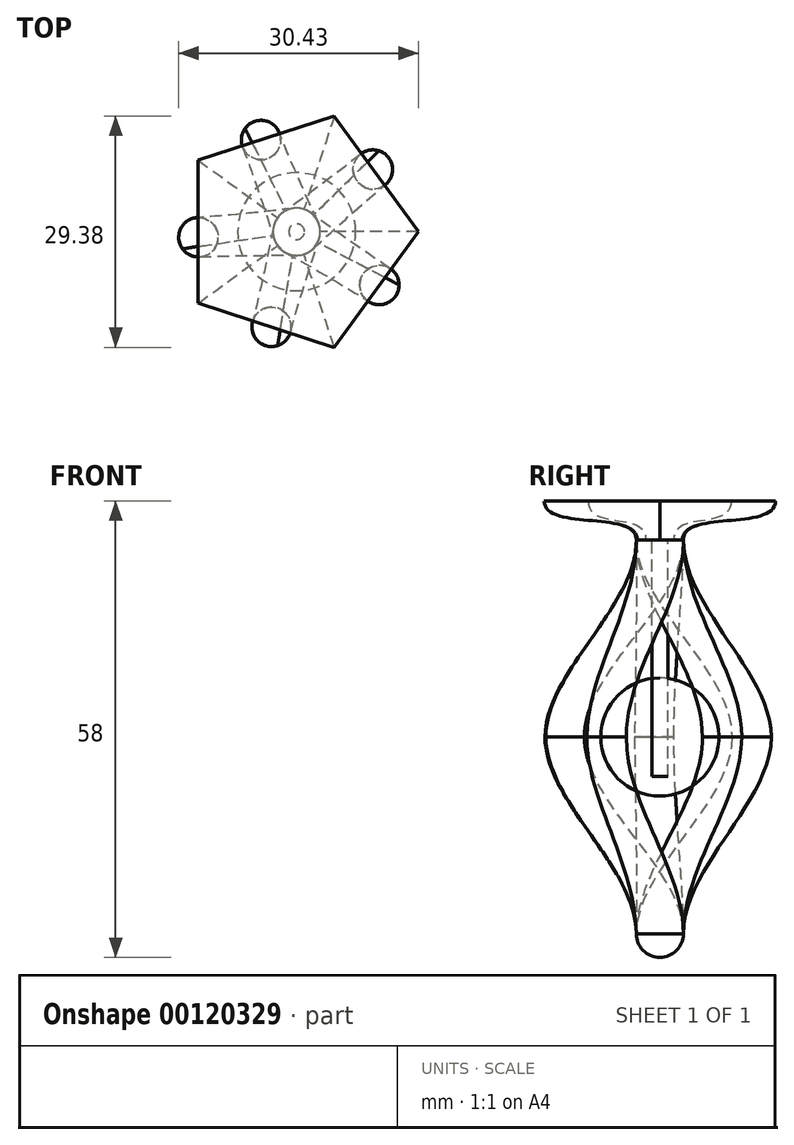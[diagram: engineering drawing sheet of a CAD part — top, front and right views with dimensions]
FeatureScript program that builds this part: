
annotation { "Feature Type Name" : "Feature", "Feature Type Description" : "" }
export const myFeature = defineFeature(function(context is Context, id is Id, definition is map)
    precondition{}
    {
        {
            var Q0;
            Q0=qCreatedBy(makeId("Top.planeOp"),FACE);
            var sketch = newSketch(context, id + "F12", { "sketchPlane" : qUnion([Q0])});
            skCircle(sketch, "E0.cCircle", {"center": v(0, 0) * mm, "radius": 12.5 * mm, "construction": true});
            skCircle(sketch, "E1", {"center": v(10.5, -6.77) * mm, "radius": 2.5 * mm});
            skSolve(sketch);
        }
        {
            var Q0;
            Q0=qCreatedBy(makeId("Top.planeOp"),FACE);
            cPlane(context, id + "F0", {"entities" : qUnion([Q0]), "cplaneType" : CPlaneType.OFFSET, "offset" : 25 * mm, "width" : 150 * mm, "height" : 150 * mm});
        }
        {
            var Q0;
            Q0=qCreatedBy(id+"F0.planeOp",FACE);
            var sketch = newSketch(context, id + "F13", { "sketchPlane" : qUnion([Q0])});
            skCircle(sketch, "E2", {"center": v(0, 0) * mm, "radius": 3 * mm});
            skSolve(sketch);
        }
        {
            var Q0;
            Q0=makeQuery(id+"F12.imprint","IMPRINT",FACE,{"disambiguationData":[TD([[makeQuery(id+"F12.imprint","IMPRINT",EDGE,{"derivedFrom":sQuery(id+"F12.wireOp",EDGE,"E1")}),1.0]])]});
            var Q1;
            Q1=makeQuery(id+"F13.imprint","IMPRINT",FACE,{"disambiguationData":[TD([[makeQuery(id+"F13.imprint","IMPRINT",EDGE,{"derivedFrom":sQuery(id+"F13.wireOp",EDGE,"E2")}),1.0]])]});
            loft(context, id + "F1", {"startCondition" : LoftEndDerivativeType.NORMAL_TO_PROFILE, "startMagnitude" : 1, "endCondition" : LoftEndDerivativeType.NORMAL_TO_PROFILE, "endMagnitude" : 1, "sheetProfilesArray" : [{ "sheetProfileEntities" : qUnion([Q0]) }, { "sheetProfileEntities" : qUnion([Q1]) }]});
        }
        {
            var Q0;
            Q0=makeQuery(id+"F1.opLoft","SWEPT_BODY",BODY,{"disambiguationData":[OSD([makeQuery(id+"F12.imprint","IMPRINT",FACE,{"disambiguationData":[TD([[makeQuery(id+"F12.imprint","IMPRINT",EDGE,{"derivedFrom":sQuery(id+"F12.wireOp",EDGE,"E1")}),1.0]])]}),makeQuery(id+"F13.imprint","IMPRINT",FACE,{"disambiguationData":[TD([[makeQuery(id+"F13.imprint","IMPRINT",EDGE,{"derivedFrom":sQuery(id+"F13.wireOp",EDGE,"E2")}),1.0]])]})])]});
            var Q1;
            Q1=sQuery(id+"F12.wireOp",EDGE,"E0.cCircle");
            circularPattern(context, id + "F2", {"entities" : qUnion([Q0]), "axis" : qUnion([Q1]), "angle" : 72 * degree, "instanceCount" : 5});
        }
        {
            var Q0;
            Q0=makeQuery(id+"F1.opLoft","SWEPT_BODY",BODY,{"disambiguationData":[OSD([makeQuery(id+"F12.imprint","IMPRINT",FACE,{"disambiguationData":[TD([[makeQuery(id+"F12.imprint","IMPRINT",EDGE,{"derivedFrom":sQuery(id+"F12.wireOp",EDGE,"E1")}),1.0]])]}),makeQuery(id+"F13.imprint","IMPRINT",FACE,{"disambiguationData":[TD([[makeQuery(id+"F13.imprint","IMPRINT",EDGE,{"derivedFrom":sQuery(id+"F13.wireOp",EDGE,"E2")}),1.0]])]})])]});
            var Q1;
            Q1=makeQuery(id+"F2.opPattern","COPY",BODY,{"derivedFrom":makeQuery(id+"F1.opLoft","SWEPT_BODY",BODY,{"disambiguationData":[OSD([makeQuery(id+"F12.imprint","IMPRINT",FACE,{"disambiguationData":[TD([[makeQuery(id+"F12.imprint","IMPRINT",EDGE,{"derivedFrom":sQuery(id+"F12.wireOp",EDGE,"E1")}),1.0]])]}),makeQuery(id+"F13.imprint","IMPRINT",FACE,{"disambiguationData":[TD([[makeQuery(id+"F13.imprint","IMPRINT",EDGE,{"derivedFrom":sQuery(id+"F13.wireOp",EDGE,"E2")}),1.0]])]})])]}),"instanceName":"1"});
            var Q2;
            Q2=makeQuery(id+"F2.opPattern","COPY",BODY,{"derivedFrom":makeQuery(id+"F1.opLoft","SWEPT_BODY",BODY,{"disambiguationData":[OSD([makeQuery(id+"F12.imprint","IMPRINT",FACE,{"disambiguationData":[TD([[makeQuery(id+"F12.imprint","IMPRINT",EDGE,{"derivedFrom":sQuery(id+"F12.wireOp",EDGE,"E1")}),1.0]])]}),makeQuery(id+"F13.imprint","IMPRINT",FACE,{"disambiguationData":[TD([[makeQuery(id+"F13.imprint","IMPRINT",EDGE,{"derivedFrom":sQuery(id+"F13.wireOp",EDGE,"E2")}),1.0]])]})])]}),"instanceName":"4"});
            var Q3;
            Q3=makeQuery(id+"F2.opPattern","COPY",BODY,{"derivedFrom":makeQuery(id+"F1.opLoft","SWEPT_BODY",BODY,{"disambiguationData":[OSD([makeQuery(id+"F12.imprint","IMPRINT",FACE,{"disambiguationData":[TD([[makeQuery(id+"F12.imprint","IMPRINT",EDGE,{"derivedFrom":sQuery(id+"F12.wireOp",EDGE,"E1")}),1.0]])]}),makeQuery(id+"F13.imprint","IMPRINT",FACE,{"disambiguationData":[TD([[makeQuery(id+"F13.imprint","IMPRINT",EDGE,{"derivedFrom":sQuery(id+"F13.wireOp",EDGE,"E2")}),1.0]])]})])]}),"instanceName":"3"});
            var Q4;
            Q4=makeQuery(id+"F2.opPattern","COPY",BODY,{"derivedFrom":makeQuery(id+"F1.opLoft","SWEPT_BODY",BODY,{"disambiguationData":[OSD([makeQuery(id+"F12.imprint","IMPRINT",FACE,{"disambiguationData":[TD([[makeQuery(id+"F12.imprint","IMPRINT",EDGE,{"derivedFrom":sQuery(id+"F12.wireOp",EDGE,"E1")}),1.0]])]}),makeQuery(id+"F13.imprint","IMPRINT",FACE,{"disambiguationData":[TD([[makeQuery(id+"F13.imprint","IMPRINT",EDGE,{"derivedFrom":sQuery(id+"F13.wireOp",EDGE,"E2")}),1.0]])]})])]}),"instanceName":"2"});
            var Q5;
            Q5=qCreatedBy(makeId("Top.planeOp"),FACE);
            mirror(context, id + "F14", {"entities" : qUnion([Q0, Q1, Q2, Q3, Q4]), "mirrorPlane" : qUnion([Q5])});
        }
        {
            var Q0;
            Q0=qCreatedBy(makeId("Right.planeOp"),FACE);
            var sketch = newSketch(context, id + "F3", { "sketchPlane" : qUnion([Q0])});
            skLineSegment(sketch, "E3", {"start": v(0, 29.68) * mm, "end": v(0, -30.32) * mm});
            skSolve(sketch);
        }
        {
            var Q0;
            Q0=qCreatedBy(makeId("Right.planeOp"),FACE);
            var sketch = newSketch(context, id + "F15", { "sketchPlane" : qUnion([Q0])});
            skEllipticalArc(sketch, "E4", {});
            skLineSegment(sketch, "E5", {"start": v(0, 7.5) * mm, "end": v(0, -7.5) * mm});
            const initialGuessFycGdjQH3IecEFOBE_1  = {"E4": [0, 0, 0, 1, 0.0075, 0.0075, 0, 3.141592653589793]};
            skSetInitialGuess(sketch, initialGuessFycGdjQH3IecEFOBE_1);
            skSolve(sketch);
        }
        {
            var Q0;
            Q0=makeQuery(id+"F15.imprint","IMPRINT",FACE,{"disambiguationData":[TD([[makeQuery(id+"F15.imprint","IMPRINT",EDGE,{"derivedFrom":sQuery(id+"F15.wireOp",EDGE,"E4")}),1.0]])]});
            var Q1;
            Q1=sQuery(id+"F3.wireOp",EDGE,"E3");
            revolve(context, id + "F4", {"entities" : qUnion([Q0]), "axis" : qUnion([Q1]), "revolveType" : RevolveType.FULL});
        }
        {
            var Q0;
            Q0=makeQuery(id+"F2.opPattern","COPY",FACE,{"derivedFrom":makeQuery(id+"F1.opLoft","CAP_FACE",FACE,{"disambiguationData":[OSD([makeQuery(id+"F13.imprint","IMPRINT",FACE,{"disambiguationData":[TD([[makeQuery(id+"F13.imprint","IMPRINT",EDGE,{"derivedFrom":sQuery(id+"F13.wireOp",EDGE,"E2")}),1.0]])]})])],"isStart":true}),"instanceName":"1"});
            var sketch = newSketch(context, id + "F5", { "sketchPlane" : qUnion([Q0])});
            skCircle(sketch, "E6", {"center": v(0, 0) * mm, "radius": 1 * mm});
            skSolve(sketch);
        }
        {
            var Q0;
            Q0=qCreatedBy(id+"F0.planeOp",FACE);
            cPlane(context, id + "F6", {"entities" : qUnion([Q0]), "cplaneType" : CPlaneType.OFFSET, "offset" : 5 * mm, "width" : 150 * mm, "height" : 150 * mm});
        }
        {
            var Q0;
            Q0=qCreatedBy(id+"F6.planeOp",FACE);
            var sketch = newSketch(context, id + "F7", { "sketchPlane" : qUnion([Q0])});
            skCircle(sketch, "E7.cCircle", {"center": v(0, 0) * mm, "radius": 12.5 * mm, "construction": true});
            skLineSegment(sketch, "E7.0", {"start": v(-12.5, -9.08) * mm, "end": v(-12.5, 9.08) * mm});
            skLineSegment(sketch, "E7.1", {"start": v(-12.5, 9.08) * mm, "end": v(4.77, 14.7) * mm});
            skLineSegment(sketch, "E7.2", {"start": v(4.77, 14.7) * mm, "end": v(15.45, 0) * mm});
            skLineSegment(sketch, "E7.3", {"start": v(15.45, 0) * mm, "end": v(4.77, -14.7) * mm});
            skLineSegment(sketch, "E7.4", {"start": v(4.77, -14.7) * mm, "end": v(-12.5, -9.08) * mm});
            skPoint(sketch, "E7.0.midPoint", {"position": v(-12.5, 0) * mm});
            skSolve(sketch);
        }
        {
            var Q0;
            Q0 = qSketchRegion(id + "F7", true);
            var Q1;
            Q1=makeQuery(id+"F2.opPattern","COPY",FACE,{"derivedFrom":makeQuery(id+"F1.opLoft","CAP_FACE",FACE,{"disambiguationData":[OSD([makeQuery(id+"F13.imprint","IMPRINT",FACE,{"disambiguationData":[TD([[makeQuery(id+"F13.imprint","IMPRINT",EDGE,{"derivedFrom":sQuery(id+"F13.wireOp",EDGE,"E2")}),1.0]])]})])],"isStart":true}),"instanceName":"3"});
            loft(context, id + "F8", {"startCondition" : LoftEndDerivativeType.NORMAL_TO_PROFILE, "startMagnitude" : 2, "endCondition" : LoftEndDerivativeType.NORMAL_TO_PROFILE, "endMagnitude" : 2, "sheetProfilesArray" : [{ "sheetProfileEntities" : qUnion([Q0]) }, { "sheetProfileEntities" : qUnion([Q1]) }]});
        }
        {
            var Q0;
            Q0=qCreatedBy(makeId("Front.planeOp"),FACE);
            var sketch = newSketch(context, id + "F9", { "sketchPlane" : qUnion([Q0])});
            skLineSegment(sketch, "E8", {"start": v(0, -25) * mm, "end": v(0, -28) * mm});
            skLineSegment(sketch, "E9", {"start": v(0, -25) * mm, "end": v(3, -25) * mm});
            skArc(sketch, "E10", {"start": v(0, -28) * mm, "mid": v(2.12, -27.12) * mm, "end": v(3, -25) * mm});
            skSolve(sketch);
        }
        {
            var Q0;
            Q0=makeQuery(id+"F9.imprint","IMPRINT",FACE,{"disambiguationData":[TD([[makeQuery(id+"F9.imprint","IMPRINT",EDGE,{"derivedFrom":sQuery(id+"F9.wireOp",EDGE,"E8")}),1.0]])]});
            var Q1;
            Q1=sQuery(id+"F9.wireOp",EDGE,"E8");
            revolve(context, id + "F10", {"entities" : qUnion([Q0]), "axis" : qUnion([Q1]), "revolveType" : RevolveType.FULL});
        }
        {
            var Q0;
            Q0 = qSketchRegion(id + "F5", true);
            extrude(context, id + "F11", {"entities" : qUnion([Q0]), "oppositeDirection" : true, "depth" : 30 * mm});
        }
    });
